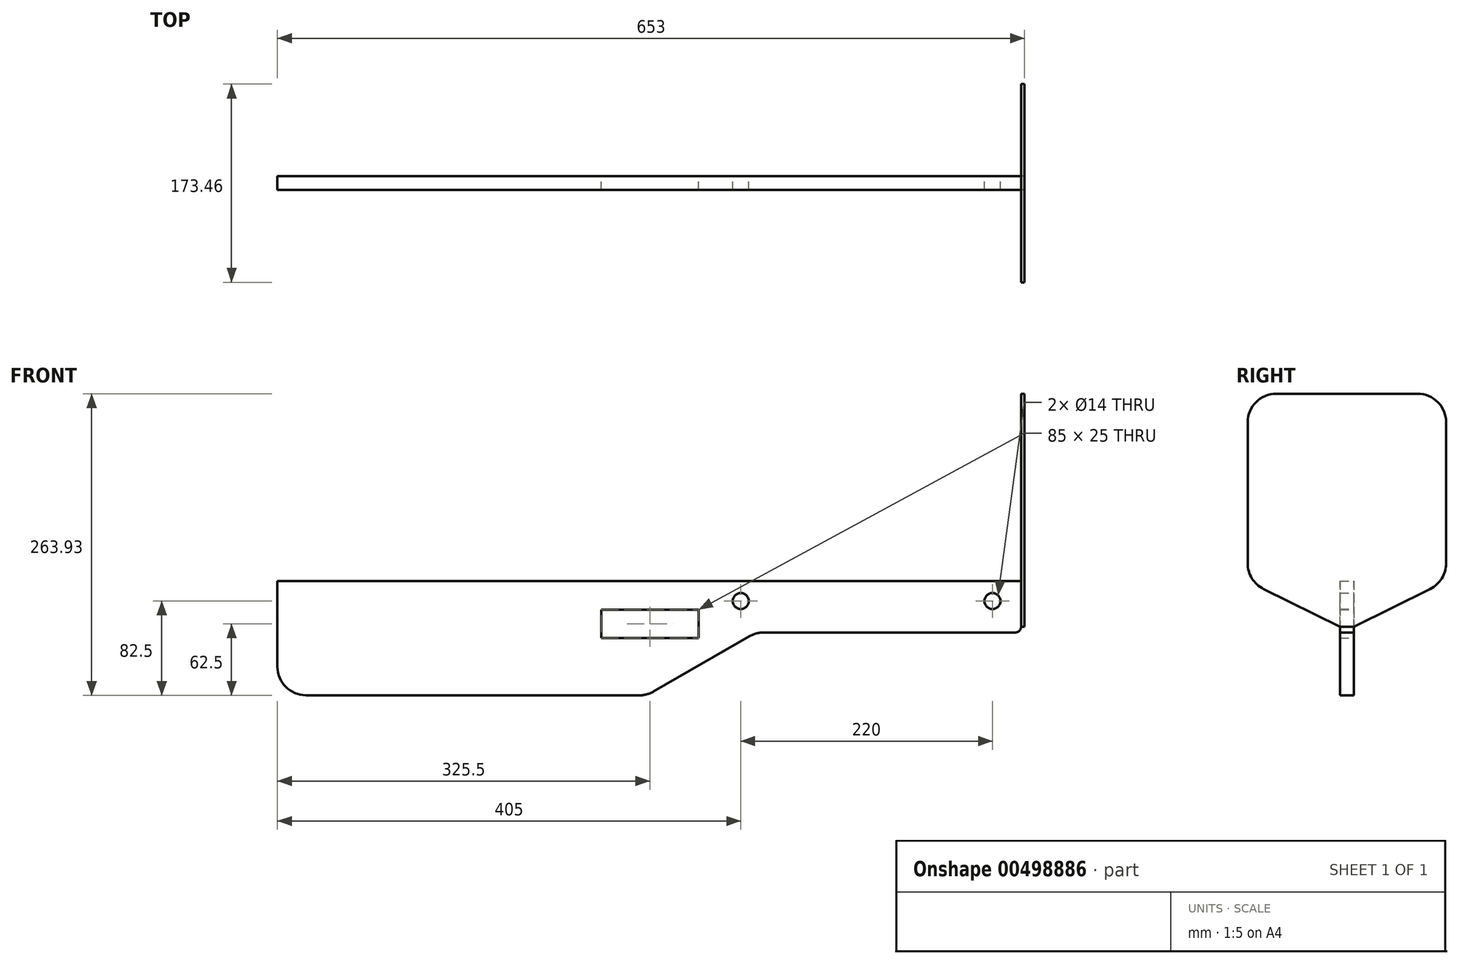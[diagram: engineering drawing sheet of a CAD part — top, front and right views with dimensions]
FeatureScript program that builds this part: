
annotation { "Feature Type Name" : "Feature", "Feature Type Description" : "" }
export const myFeature = defineFeature(function(context is Context, id is Id, definition is map)
    precondition{}
    {
        {
            var Q0;
            Q0=qCreatedBy(makeId("Front.planeOp"),FACE);
            var sketch = newSketch(context, id + "F0", { "sketchPlane" : qUnion([Q0])});
            skLineSegment(sketch, "E0.bottom", {"start": v(0, 0) * mm, "end": v(285, 0) * mm});
            skLineSegment(sketch, "E0.top", {"start": v(60, -45) * mm, "end": v(280, -45) * mm});
            skLineSegment(sketch, "E0.right", {"start": v(285, 0) * mm, "end": v(285, -40) * mm});
            skCircle(sketch, "E1", {"center": v(40, -17.5) * mm, "radius": 7 * mm});
            skCircle(sketch, "E2", {"center": v(260, -17.5) * mm, "radius": 7 * mm});
            skPoint(sketch, "E3.visualSharp", {"position": v(0, -45) * mm});
            skPoint(sketch, "E4.visualSharp", {"position": v(285, -45) * mm});
            skArc(sketch, "E4.filletArc", {"start": v(280, -45) * mm, "mid": v(283.54, -43.54) * mm, "end": v(285, -40) * mm});
            skLineSegment(sketch, "E5", {"start": v(47.5, -48.35) * mm, "end": v(-36.16, -96.65) * mm});
            skLineSegment(sketch, "E6", {"start": v(-48.66, -100) * mm, "end": v(-340, -100) * mm});
            skLineSegment(sketch, "E7", {"start": v(-365, -75) * mm, "end": v(-365, 0) * mm});
            skLineSegment(sketch, "E8", {"start": v(-365, 0) * mm, "end": v(0, 0) * mm});
            skPoint(sketch, "E9.visualSharp", {"position": v(-365, -100) * mm});
            skArc(sketch, "E9.filletArc", {"start": v(-365, -75) * mm, "mid": v(-357.68, -92.68) * mm, "end": v(-340, -100) * mm});
            skPoint(sketch, "E10.visualSharp", {"position": v(-41.96, -100) * mm});
            skArc(sketch, "E10.filletArc", {"start": v(-48.66, -100) * mm, "mid": v(-42.19, -99.15) * mm, "end": v(-36.16, -96.65) * mm});
            skPoint(sketch, "E11.visualSharp", {"position": v(53.3, -45) * mm});
            skArc(sketch, "E11.filletArc", {"start": v(60, -45) * mm, "mid": v(53.53, -45.85) * mm, "end": v(47.5, -48.35) * mm});
            skSolve(sketch);
        }
        {
            var Q0;
            Q0=makeQuery(id+"F0.imprint","IMPRINT",FACE,{"disambiguationData":[TD([[makeQuery(id+"F0.imprint","IMPRINT",EDGE,{"derivedFrom":sQuery(id+"F0.wireOp",EDGE,"E0.bottom")}),-1.0]])]});
            extrude(context, id + "F1", {"entities" : qUnion([Q0]), "depth" : 12 * mm});
        }
        {
            var Q0;
            Q0=makeQuery(id+"F1.opExtrude","CAP_FACE",FACE,{"disambiguationData":[OSD([sQuery(id+"F0.wireOp",EDGE,"E0.bottom"),sQuery(id+"F0.wireOp",EDGE,"E0.top"),sQuery(id+"F0.wireOp",EDGE,"E0.right"),sQuery(id+"F0.wireOp",EDGE,"E1"),sQuery(id+"F0.wireOp",EDGE,"E2"),sQuery(id+"F0.wireOp",EDGE,"E4.filletArc"),sQuery(id+"F0.wireOp",EDGE,"E5"),sQuery(id+"F0.wireOp",EDGE,"E6"),sQuery(id+"F0.wireOp",EDGE,"E7"),sQuery(id+"F0.wireOp",EDGE,"E8"),sQuery(id+"F0.wireOp",EDGE,"E9.filletArc"),sQuery(id+"F0.wireOp",EDGE,"E10.filletArc"),sQuery(id+"F0.wireOp",EDGE,"E11.filletArc")])],"isStart":true});
            var sketch = newSketch(context, id + "F2", { "sketchPlane" : qUnion([Q0])});
            skLineSegment(sketch, "E12.bottom", {"start": v(-3, -25) * mm, "end": v(82, -25) * mm});
            skLineSegment(sketch, "E12.top", {"start": v(-3, -50) * mm, "end": v(82, -50) * mm});
            skLineSegment(sketch, "E12.left", {"start": v(-3, -25) * mm, "end": v(-3, -50) * mm});
            skLineSegment(sketch, "E12.right", {"start": v(82, -25) * mm, "end": v(82, -50) * mm});
            skSolve(sketch);
        }
        {
            var Q0;
            Q0=makeQuery(id+"F2.imprint","IMPRINT",FACE,{"disambiguationData":[TD([[makeQuery(id+"F2.imprint","IMPRINT",EDGE,{"derivedFrom":sQuery(id+"F2.wireOp",EDGE,"E12.bottom")}),-1.0]])]});
            extrude(context, id + "F3", {"entities" : qUnion([Q0]), "operationType" : NewBodyOperationType.REMOVE, "oppositeDirection" : true, "depth" : 25 * mm});
        }
        {
            var Q0;
            Q0=makeQuery(id+"F1.opExtrude","SWEPT_FACE",FACE,{"disambiguationData":[OSD([sQuery(id+"F0.wireOp",EDGE,"E0.right")])]});
            var sketch = newSketch(context, id + "F4", { "sketchPlane" : qUnion([Q0])});
            skLineSegment(sketch, "E13", {"start": v(-6, 0) * mm, "end": v(-6, 45.53) * mm, "construction": true});
            skLineSegment(sketch, "E14", {"start": v(-6, -40) * mm, "end": v(-12, -40) * mm});
            skLineSegment(sketch, "E15", {"start": v(-12, -40) * mm, "end": v(-78.83, -6.89) * mm});
            skLineSegment(sketch, "E16", {"start": v(-92.73, 15.51) * mm, "end": v(-92.73, 138.93) * mm});
            skLineSegment(sketch, "E17", {"start": v(-67.73, 163.93) * mm, "end": v(0, 163.93) * mm});
            skPoint(sketch, "E18.visualSharp", {"position": v(-92.73, 163.93) * mm});
            skArc(sketch, "E18.filletArc", {"start": v(-67.73, 163.93) * mm, "mid": v(-85.4, 156.6) * mm, "end": v(-92.73, 138.93) * mm});
            skPoint(sketch, "E19.visualSharp", {"position": v(-92.73, 0) * mm});
            skArc(sketch, "E19.filletArc", {"start": v(-92.73, 15.51) * mm, "mid": v(-88.97, 2.33) * mm, "end": v(-78.83, -6.89) * mm});
            skArc(sketch, "E20.MirrorCS", {"start": v(80.73, 15.51) * mm, "mid": v(76.97, 2.33) * mm, "end": v(66.83, -6.89) * mm});
            skLineSegment(sketch, "E21.MirrorCS", {"start": v(-6, -40) * mm, "end": v(0, -40) * mm});
            skArc(sketch, "E22.MirrorCS", {"start": v(55.73, 163.93) * mm, "mid": v(73.4, 156.6) * mm, "end": v(80.73, 138.93) * mm});
            skLineSegment(sketch, "E23.MirrorCS", {"start": v(55.73, 163.93) * mm, "end": v(-12, 163.93) * mm});
            skLineSegment(sketch, "E24.MirrorCS", {"start": v(0, -40) * mm, "end": v(66.83, -6.89) * mm});
            skPoint(sketch, "E25.MirrorP", {"position": v(80.73, 0) * mm});
            skLineSegment(sketch, "E26.MirrorCS", {"start": v(80.73, 15.51) * mm, "end": v(80.73, 138.93) * mm});
            skPoint(sketch, "E27.MirrorP", {"position": v(80.73, 163.93) * mm});
            skSolve(sketch);
        }
        {
            var Q0;
            Q0 = qSketchRegion(id + "F4", true);
            extrude(context, id + "F5", {"entities" : qUnion([Q0]), "operationType" : NewBodyOperationType.ADD, "depth" : 3 * mm});
        }
    });
